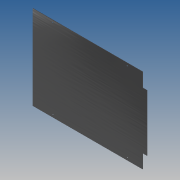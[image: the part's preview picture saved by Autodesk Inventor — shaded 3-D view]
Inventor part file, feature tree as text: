
AUTODESK INVENTOR PART (.ipt)
format: ipt  version: 2019 (Build 230136000, 136)  size: 122,880 bytes
history: native  units: mm
features: sketch x3, extrude x2, projected_geometry x2, hole x1
ambient origin geometry x8: Origin, YZ Plane, XZ Plane, XY Plane, X Axis, Y Axis, Z Axis, Center Point
bodies: Solid1 (feature_tree)
feature tree (8):
  extrude  "Extrusion1"  Depth=575.0mm
  extrude  "Extrusion2"  Depth=22.0mm
  hole  "Hole1"  [1 undecoded]
  sketch  "Sketch2"  dims[d0=425.0mm d1=575.0mm]
  sketch  "Sketch3"  dims[d2=2.0mm d3=0.0mm d4=22.0mm]
  projected_geometry  "Projected Loop1"
  sketch  "Sketch4"  dims[d5=70.0mm d6=70.0mm d7=2.0mm d8=0.0mm d9=12.5mm d10=12.5mm d11=100.0mm d12=100.0mm d13=100.0mm d14=100.0mm d15=6.0mm d16=8.0mm d17=4.0mm d18=2.0mm d19=90.0deg d20=10.0mm d21=20.594885mm]
  projected_geometry  "Projected Loop2"
note: 1 required parameter value undecoded (feature->parameter linkage not recoverable at this tier; creation-order binding heuristic only, values carry confidence <= 0.55)
